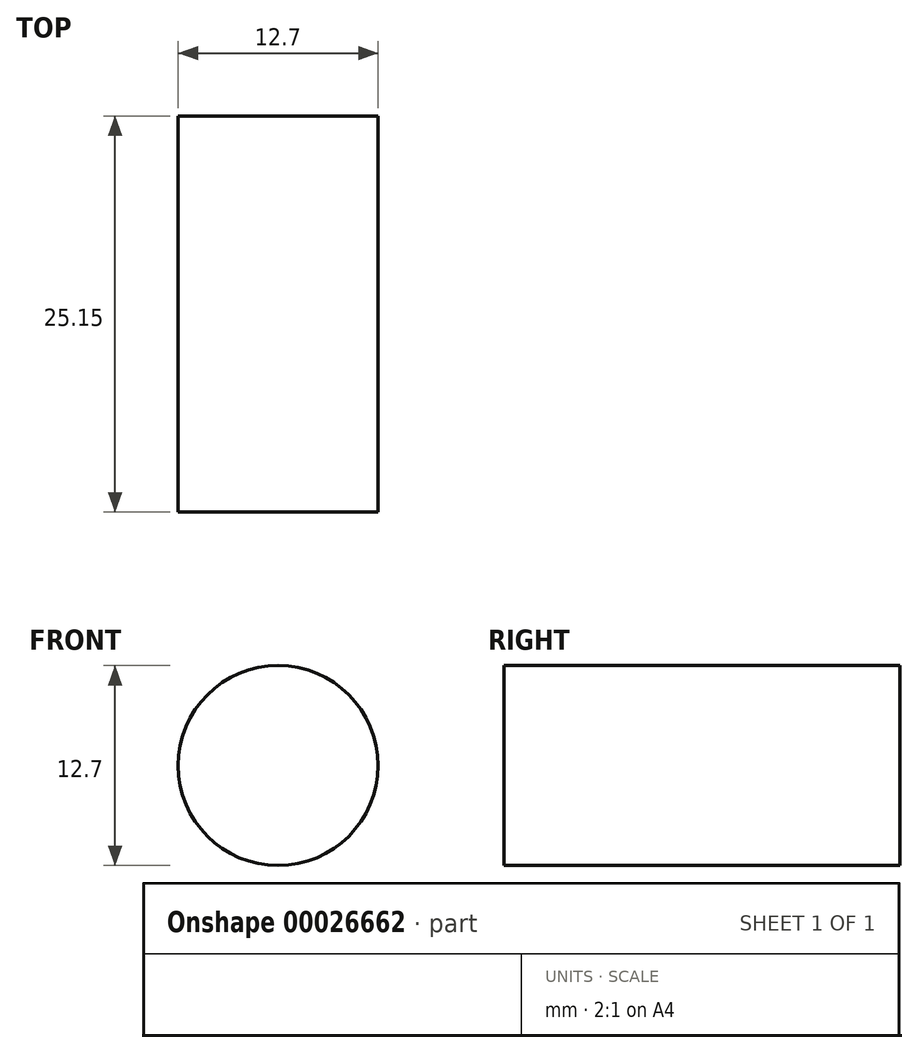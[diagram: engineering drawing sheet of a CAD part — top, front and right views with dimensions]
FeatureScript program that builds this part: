
annotation { "Feature Type Name" : "Feature", "Feature Type Description" : "" }
export const myFeature = defineFeature(function(context is Context, id is Id, definition is map)
    precondition{}
    {
        {
            var Q0;
            Q0=qCreatedBy(makeId("Front.planeOp"),FACE);
            var sketch = newSketch(context, id + "F0", { "sketchPlane" : qUnion([Q0])});
            skCircle(sketch, "E0", {"center": v(0, 0.65) * mm, "radius": 6.35 * mm});
            skSolve(sketch);
        }
        {
            var Q0;
            Q0=makeQuery(id+"F0.imprint","IMPRINT",FACE,{"disambiguationData":[TD([[makeQuery(id+"F0.imprint","IMPRINT",EDGE,{"derivedFrom":sQuery(id+"F0.wireOp",EDGE,"E0")}),1.0]])]});
            extrude(context, id + "F1", {"entities" : qUnion([Q0]), "depth" : 25.15 * mm});
        }
    });
